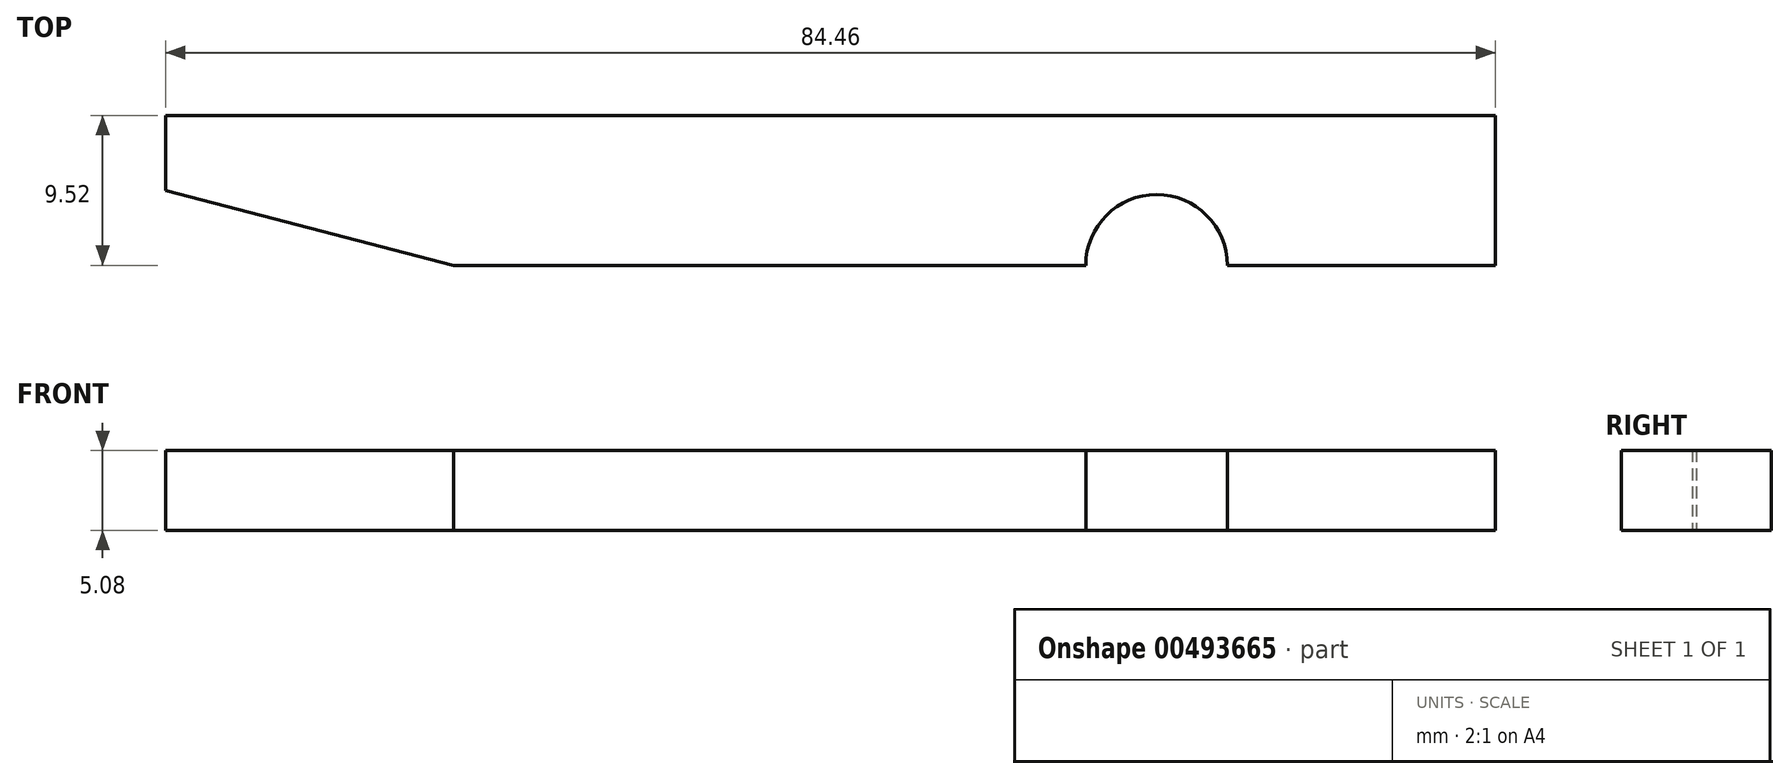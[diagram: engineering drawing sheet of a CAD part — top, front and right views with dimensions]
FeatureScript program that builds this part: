
annotation { "Feature Type Name" : "Feature", "Feature Type Description" : "" }
export const myFeature = defineFeature(function(context is Context, id is Id, definition is map)
    precondition{}
    {
        {
            var Q0;
            Q0=qCreatedBy(makeId("Top.planeOp"),FACE);
            var sketch = newSketch(context, id + "F0", { "sketchPlane" : qUnion([Q0])});
            skLineSegment(sketch, "E0.bottom", {"start": v(-47.37, 4.94) * mm, "end": v(-17.2, 4.94) * mm});
            skLineSegment(sketch, "E0.top", {"start": v(-29.09, -4.58) * mm, "end": v(11.06, -4.58) * mm});
            skLineSegment(sketch, "E0.left", {"start": v(-47.37, 4.94) * mm, "end": v(-47.37, 0.18) * mm});
            skLineSegment(sketch, "E0.right", {"start": v(37.09, 4.94) * mm, "end": v(37.09, -4.58) * mm});
            skLineSegment(sketch, "E1.trimOffspring", {"start": v(19.3, 4.94) * mm, "end": v(37.09, 4.94) * mm});
            skLineSegment(sketch, "E2", {"start": v(-17.2, 4.94) * mm, "end": v(12.96, 4.94) * mm});
            skLineSegment(sketch, "E3", {"start": v(-47.37, 0.18) * mm, "end": v(-29.09, -4.58) * mm});
            skLineSegment(sketch, "E4", {"start": v(12.96, 4.94) * mm, "end": v(19.3, 4.94) * mm});
            skArc(sketch, "E5", {"start": v(20.06, -4.58) * mm, "mid": v(15.56, -0.08) * mm, "end": v(11.06, -4.58) * mm});
            skLineSegment(sketch, "E6.trimOffspring", {"start": v(20.06, -4.58) * mm, "end": v(37.09, -4.58) * mm});
            skPoint(sketch, "E7.start.orphan", {"position": v(11.82, -4.58) * mm});
            skPoint(sketch, "E8.trimOffspring.end.orphan", {"position": v(19.3, -4.58) * mm});
            skSolve(sketch);
        }
        {
            var Q0;
            Q0 = qSketchRegion(id + "F0", true);
            extrude(context, id + "F1", {"entities" : qUnion([Q0]), "depth" : 5.08 * mm});
        }
    });
